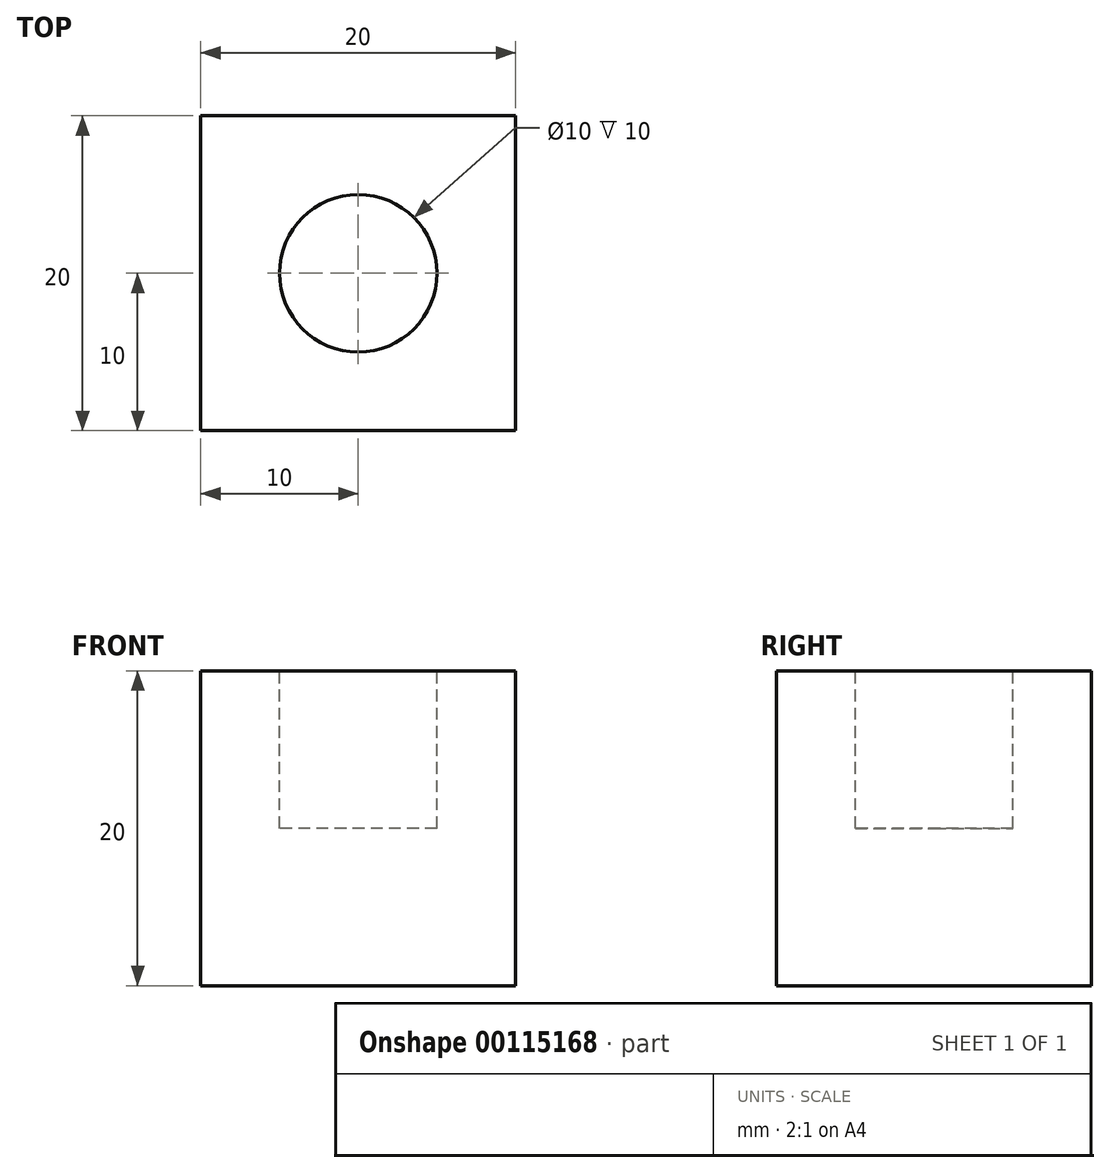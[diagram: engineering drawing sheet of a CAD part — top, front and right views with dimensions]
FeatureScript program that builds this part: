
annotation { "Feature Type Name" : "Feature", "Feature Type Description" : "" }
export const myFeature = defineFeature(function(context is Context, id is Id, definition is map)
    precondition{}
    {
        {
            var Q0;
            Q0=qCreatedBy(makeId("Top.planeOp"),FACE);
            var sketch = newSketch(context, id + "F0", { "sketchPlane" : qUnion([Q0])});
            skLineSegment(sketch, "E0.bottom", {"start": v(10, -10) * mm, "end": v(-10, -10) * mm});
            skLineSegment(sketch, "E0.top", {"start": v(10, 10) * mm, "end": v(-10, 10) * mm});
            skLineSegment(sketch, "E0.left", {"start": v(10, -10) * mm, "end": v(10, 10) * mm});
            skLineSegment(sketch, "E0.right", {"start": v(-10, -10) * mm, "end": v(-10, 10) * mm});
            skPoint(sketch, "E0.middle", {"position": v(0, 0) * mm});
            skSolve(sketch);
        }
        {
            var Q0;
            Q0=makeQuery(id+"F0.imprint","IMPRINT",FACE,{"disambiguationData":[TD([[makeQuery(id+"F0.imprint","IMPRINT",EDGE,{"derivedFrom":sQuery(id+"F0.wireOp",EDGE,"E0.bottom")}),-1.0]])]});
            extrude(context, id + "F1", {"entities" : qUnion([Q0]), "depth" : 20 * mm});
        }
        {
            var Q0;
            Q0=makeQuery(id+"F1.opExtrude","CAP_FACE",FACE,{"disambiguationData":[OSD([sQuery(id+"F0.wireOp",EDGE,"E0.bottom"),sQuery(id+"F0.wireOp",EDGE,"E0.top"),sQuery(id+"F0.wireOp",EDGE,"E0.left"),sQuery(id+"F0.wireOp",EDGE,"E0.right")])],"isStart":false});
            var sketch = newSketch(context, id + "F2", { "sketchPlane" : qUnion([Q0])});
            skCircle(sketch, "E1", {"center": v(0, 0) * mm, "radius": 5 * mm});
            skSolve(sketch);
        }
        {
            var Q0;
            Q0=makeQuery(id+"F2.imprint","IMPRINT",FACE,{"disambiguationData":[TD([[makeQuery(id+"F2.imprint","IMPRINT",EDGE,{"derivedFrom":sQuery(id+"F2.wireOp",EDGE,"E1")}),1.0]])]});
            extrude(context, id + "F3", {"entities" : qUnion([Q0]), "operationType" : NewBodyOperationType.REMOVE, "oppositeDirection" : true, "depth" : 10 * mm});
        }
    });
